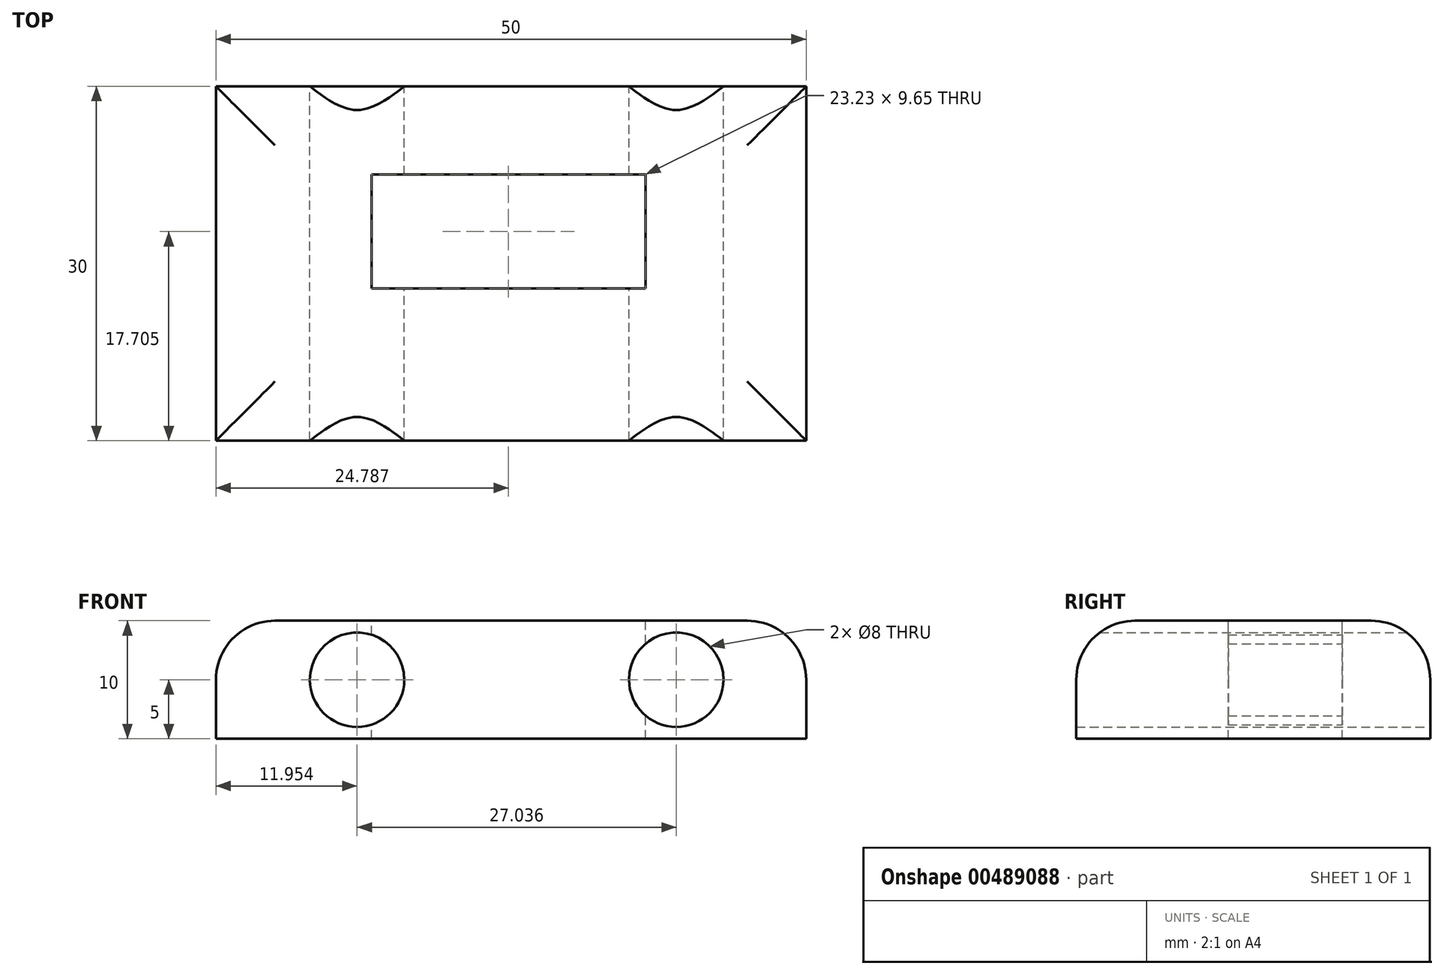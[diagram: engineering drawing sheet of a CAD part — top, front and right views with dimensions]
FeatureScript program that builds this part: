
annotation { "Feature Type Name" : "Feature", "Feature Type Description" : "" }
export const myFeature = defineFeature(function(context is Context, id is Id, definition is map)
    precondition{}
    {
        {
            var Q0;
            Q0=qCreatedBy(makeId("Front.planeOp"),FACE);
            var sketch = newSketch(context, id + "F0", { "sketchPlane" : qUnion([Q0])});
            skLineSegment(sketch, "E0.bottom", {"start": v(-25, 5) * mm, "end": v(25, 5) * mm});
            skLineSegment(sketch, "E0.top", {"start": v(-25, -5) * mm, "end": v(25, -5) * mm});
            skLineSegment(sketch, "E0.left", {"start": v(-25, 5) * mm, "end": v(-25, -5) * mm});
            skLineSegment(sketch, "E0.right", {"start": v(25, 5) * mm, "end": v(25, -5) * mm});
            skPoint(sketch, "E0.middle", {"position": v(0, 0) * mm});
            skSolve(sketch);
        }
        {
            var Q0;
            Q0=makeQuery(id+"F0.imprint","IMPRINT",FACE,{"disambiguationData":[TD([[makeQuery(id+"F0.imprint","IMPRINT",EDGE,{"derivedFrom":sQuery(id+"F0.wireOp",EDGE,"E0.bottom")}),-1.0]])]});
            extrude(context, id + "F1", {"entities" : qUnion([Q0]), "depth" : 30 * mm});
        }
        {
            var Q0;
            Q0=qCreatedBy(makeId("Front.planeOp"),FACE);
            var sketch = newSketch(context, id + "F2", { "sketchPlane" : qUnion([Q0])});
            skCircle(sketch, "E1", {"center": v(-13.05, 0) * mm, "radius": 4.04 * mm});
            skCircle(sketch, "E2", {"center": v(13.99, 0) * mm, "radius": 4.08 * mm});
            skSolve(sketch);
        }
        {
            var Q0;
            Q0=sQuery(id+"F2.wireOp",VERTEX,"E1.center");
            var Q1;
            Q1=sQuery(id+"F2.wireOp",VERTEX,"E2.center");
            var Q2;
            Q2=makeQuery(id+"F1.opExtrude","SWEPT_BODY",BODY,{"disambiguationData":[OSD([sQuery(id+"F0.wireOp",EDGE,"E0.bottom"),sQuery(id+"F0.wireOp",EDGE,"E0.top"),sQuery(id+"F0.wireOp",EDGE,"E0.left"),sQuery(id+"F0.wireOp",EDGE,"E0.right")])]});
            hole(context, id + "F3", {"style" : HoleStyle.SIMPLE, "endStyle" : HoleEndStyle.THROUGH, "oppositeDirection" : true, "holeDiameter" : 8 * mm, "isTappedThrough" : true, "tappedDepth" : 12 * mm, "tapClearance" : 3, "locations" : qUnion([Q0, Q1]), "scope" : qUnion([Q2])});
        }
        {
            var Q0;
            Q0=makeQuery(id+"F1.opExtrude","SWEPT_FACE",FACE,{"disambiguationData":[OSD([sQuery(id+"F0.wireOp",EDGE,"E0.bottom")])]});
            fillet(context, id + "F4", {"entities" : qUnion([Q0]), "radius" : 5 * mm, "tangentPropagation" : true, "allowEdgeOverflow" : false});
        }
        {
            var Q0;
            Q0=makeQuery(id+"F1.opExtrude","SWEPT_FACE",FACE,{"disambiguationData":[OSD([sQuery(id+"F0.wireOp",EDGE,"E0.bottom")])]});
            var sketch = newSketch(context, id + "F5", { "sketchPlane" : qUnion([Q0])});
            skLineSegment(sketch, "E3.bottom", {"start": v(11.4, -17.12) * mm, "end": v(-11.83, -17.12) * mm});
            skLineSegment(sketch, "E3.top", {"start": v(11.4, -7.47) * mm, "end": v(-11.83, -7.47) * mm});
            skLineSegment(sketch, "E3.left", {"start": v(11.4, -17.12) * mm, "end": v(11.4, -7.47) * mm});
            skLineSegment(sketch, "E3.right", {"start": v(-11.83, -17.12) * mm, "end": v(-11.83, -7.47) * mm});
            skSolve(sketch);
        }
        {
            var Q0;
            Q0=makeQuery(id+"F5.imprint","IMPRINT",FACE,{"disambiguationData":[TD([[makeQuery(id+"F5.imprint","IMPRINT",EDGE,{"derivedFrom":sQuery(id+"F5.wireOp",EDGE,"E3.bottom")}),-1.0]])]});
            extrude(context, id + "F6", {"entities" : qUnion([Q0]), "operationType" : NewBodyOperationType.REMOVE, "oppositeDirection" : true, "depth" : 25 * mm});
        }
    });
